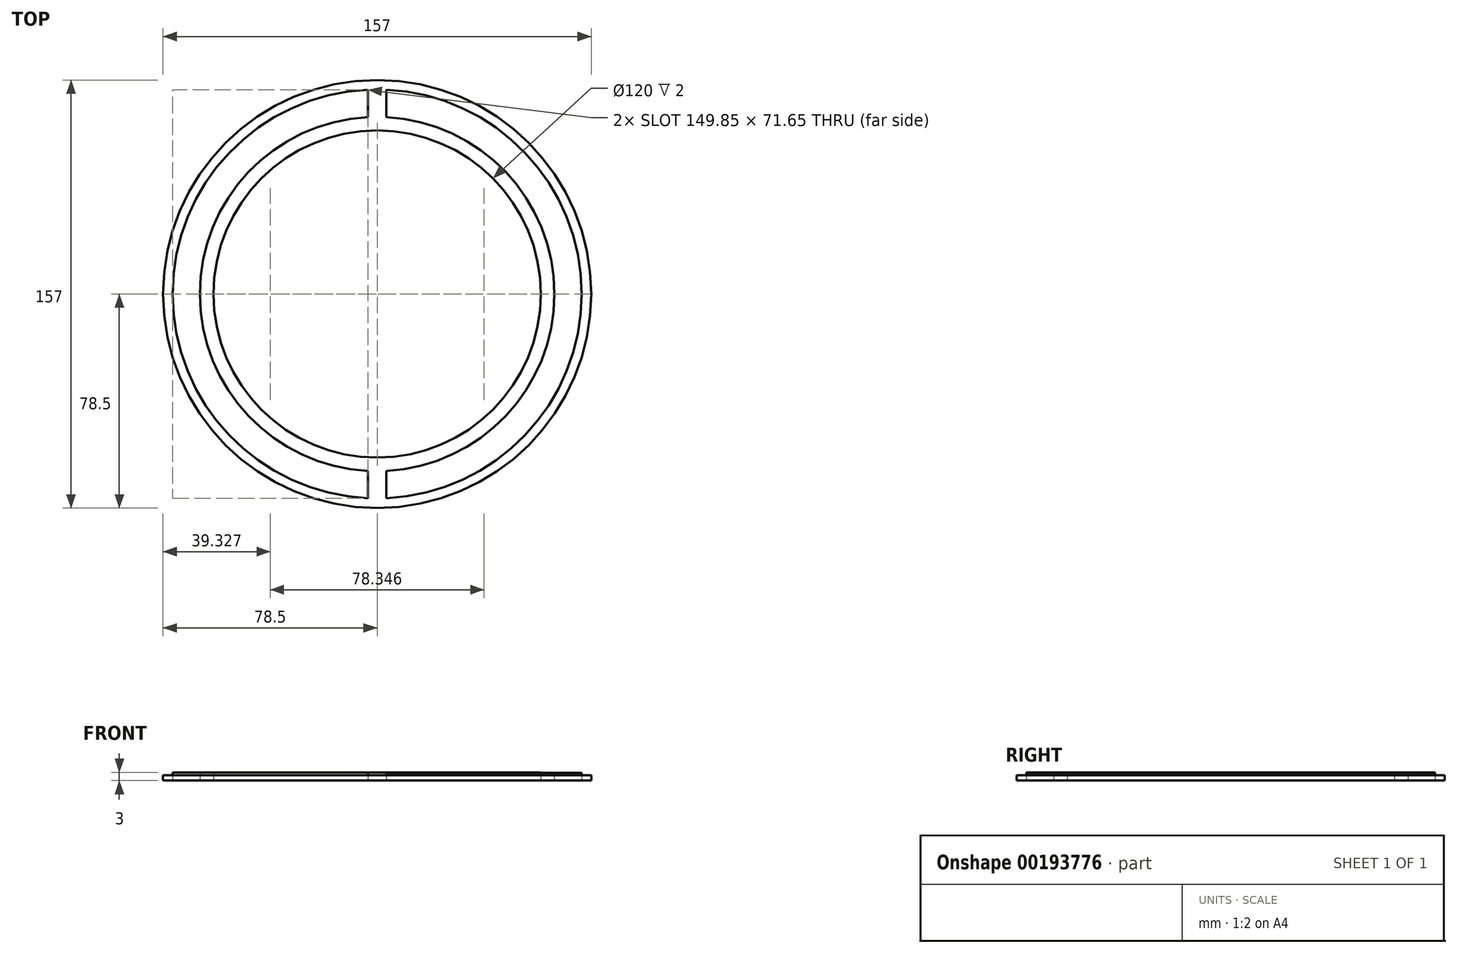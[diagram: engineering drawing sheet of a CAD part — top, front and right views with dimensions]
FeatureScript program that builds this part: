
annotation { "Feature Type Name" : "Feature", "Feature Type Description" : "" }
export const myFeature = defineFeature(function(context is Context, id is Id, definition is map)
    precondition{}
    {
        {
            var Q0;
            Q0=qCreatedBy(makeId("Top.planeOp"),FACE);
            var sketch = newSketch(context, id + "F0", { "sketchPlane" : qUnion([Q0])});
            skCircle(sketch, "E0", {"center": v(0, 0) * mm, "radius": 78.5 * mm});
            skArc(sketch, "E1", {"start": v(-3.35, 74.93) * mm, "mid": v(-75, 0) * mm, "end": v(-3.35, -74.93) * mm});
            skArc(sketch, "E2", {"start": v(3.35, -74.93) * mm, "mid": v(75, 0) * mm, "end": v(3.35, 74.93) * mm});
            skArc(sketch, "E3", {"start": v(-3.35, 64.91) * mm, "mid": v(-65, 0) * mm, "end": v(-3.35, -64.91) * mm});
            skArc(sketch, "E4", {"start": v(3.35, -64.91) * mm, "mid": v(65, 0) * mm, "end": v(3.35, 64.91) * mm});
            skLineSegment(sketch, "E5", {"start": v(-3.35, 64.91) * mm, "end": v(-3.35, 75) * mm});
            skLineSegment(sketch, "E6.MirrorCS", {"start": v(3.35, 64.91) * mm, "end": v(3.35, 75) * mm});
            skLineSegment(sketch, "E7.MirrorCS", {"start": v(3.35, -64.91) * mm, "end": v(3.35, -75) * mm});
            skLineSegment(sketch, "E8.MirrorCS", {"start": v(-3.35, -64.91) * mm, "end": v(-3.35, -75) * mm});
            skPoint(sketch, "E9.orphan", {"position": v(-0.15, 75) * mm});
            skCircle(sketch, "E10", {"center": v(0, 0) * mm, "radius": 60 * mm});
            skSolve(sketch);
        }
        {
            var Q0;
            {var subQ0=sQuery(id+"F0.wireOp",EDGE,"E1");Q0=makeQuery(id+"F0.imprint","IMPRINT",FACE,{"disambiguationData":[TD([[makeQuery(id+"F0.imprint","IMPRINT",EDGE,{"derivedFrom":subQ0}),1.0]])]});}
            extrude(context, id + "F1", {"entities" : qUnion([Q0]), "depth" : 3 * mm});
        }
        {
            var Q0;
            {var subQ0=sQuery(id+"F0.wireOp",EDGE,"E2");Q0=makeQuery(id+"F0.imprint","IMPRINT",FACE,{"disambiguationData":[TD([[makeQuery(id+"F0.imprint","IMPRINT",EDGE,{"derivedFrom":subQ0}),1.0]])]});}
            extrude(context, id + "F2", {"entities" : qUnion([Q0]), "depth" : 2.9 * mm});
        }
        {
            var Q0;
            Q0=makeQuery(id+"F0.imprint","IMPRINT",FACE,{"disambiguationData":[TD([[makeQuery(id+"F0.imprint","IMPRINT",EDGE,{"derivedFrom":sQuery(id+"F0.wireOp",EDGE,"E10")}),1.0]])]});
            extrude(context, id + "F3", {"entities" : qUnion([Q0]), "depth" : 3 * mm});
        }
        {
            var Q0;
            Q0=makeQuery(id+"F0.imprint","IMPRINT",FACE,{"disambiguationData":[TD([[makeQuery(id+"F0.imprint","IMPRINT",EDGE,{"derivedFrom":sQuery(id+"F0.wireOp",EDGE,"E0")}),1.0]])]});
            extrude(context, id + "F4", {"entities" : qUnion([Q0]), "depth" : 2 * mm});
        }
    });
